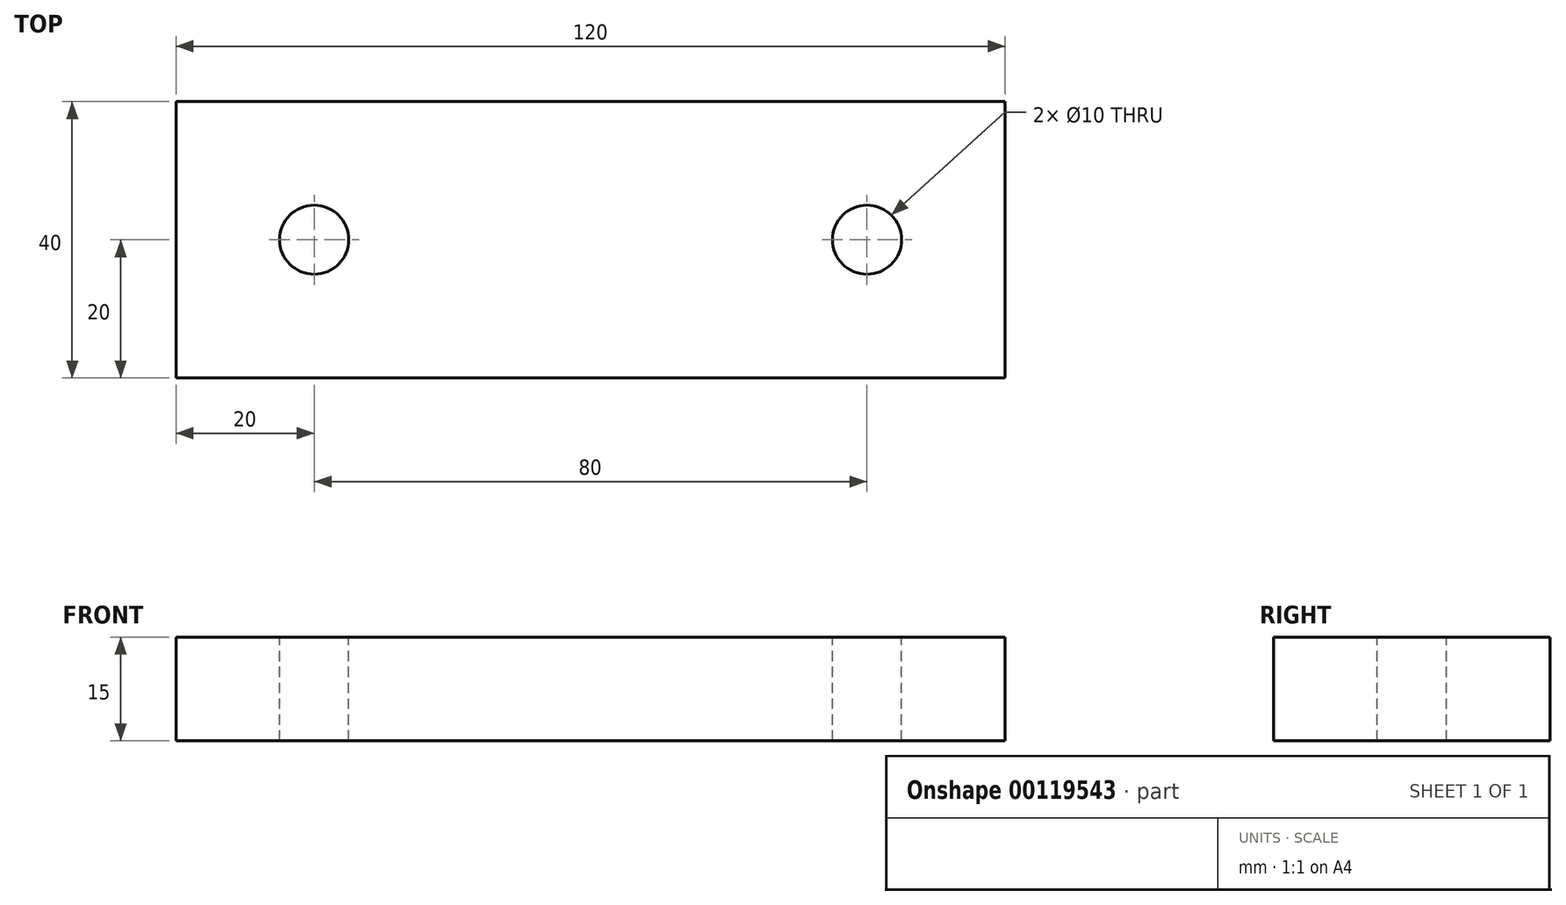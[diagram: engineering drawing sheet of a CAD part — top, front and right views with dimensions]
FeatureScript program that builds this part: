
annotation { "Feature Type Name" : "Feature", "Feature Type Description" : "" }
export const myFeature = defineFeature(function(context is Context, id is Id, definition is map)
    precondition{}
    {
        {
            var Q0;
            Q0=qCreatedBy(makeId("Top.planeOp"),FACE);
            var sketch = newSketch(context, id + "F0", { "sketchPlane" : qUnion([Q0])});
            skLineSegment(sketch, "E0.bottom", {"start": v(-60, -20) * mm, "end": v(60, -20) * mm});
            skLineSegment(sketch, "E0.top", {"start": v(-60, 20) * mm, "end": v(60, 20) * mm});
            skLineSegment(sketch, "E0.left", {"start": v(-60, -20) * mm, "end": v(-60, 20) * mm});
            skLineSegment(sketch, "E0.right", {"start": v(60, -20) * mm, "end": v(60, 20) * mm});
            skPoint(sketch, "E0.middle", {"position": v(0, 0) * mm});
            skCircle(sketch, "E1", {"center": v(-40, 0) * mm, "radius": 5 * mm});
            skCircle(sketch, "E2", {"center": v(40, 0) * mm, "radius": 5 * mm});
            skSolve(sketch);
        }
        {
            var Q0;
            Q0=makeQuery(id+"F0.imprint","IMPRINT",FACE,{"disambiguationData":[TD([[makeQuery(id+"F0.imprint","IMPRINT",EDGE,{"derivedFrom":sQuery(id+"F0.wireOp",EDGE,"E0.bottom")}),1.0]])]});
            extrude(context, id + "F1", {"entities" : qUnion([Q0]), "oppositeDirection" : true, "depth" : 15 * mm});
        }
    });
